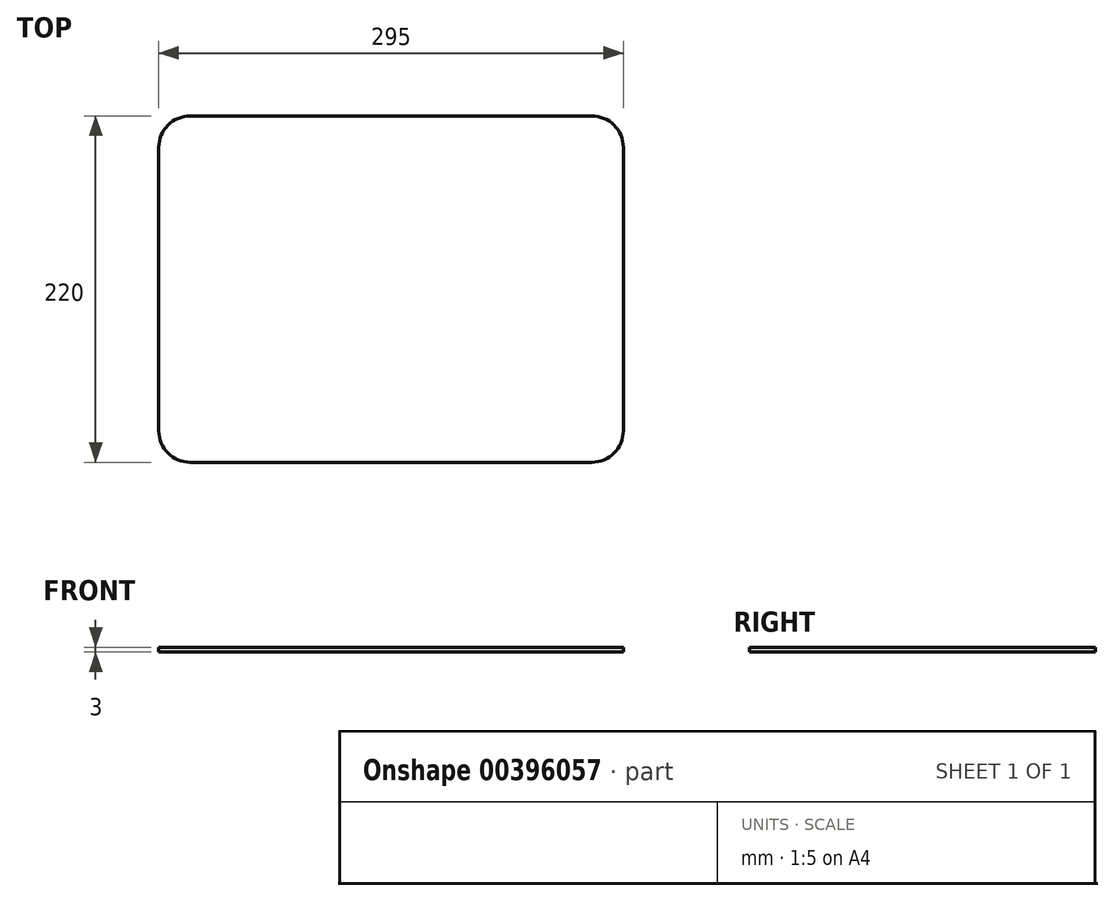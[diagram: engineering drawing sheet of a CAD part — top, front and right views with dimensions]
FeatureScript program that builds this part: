
annotation { "Feature Type Name" : "Feature", "Feature Type Description" : "" }
export const myFeature = defineFeature(function(context is Context, id is Id, definition is map)
    precondition{}
    {
        {
            var Q0;
            Q0=qCreatedBy(makeId("Top.planeOp"),FACE);
            var sketch = newSketch(context, id + "F0", { "sketchPlane" : qUnion([Q0])});
            skLineSegment(sketch, "E0.bottom", {"start": v(-127.5, 110) * mm, "end": v(127.5, 110) * mm});
            skLineSegment(sketch, "E0.top", {"start": v(-127.5, -110) * mm, "end": v(127.5, -110) * mm});
            skLineSegment(sketch, "E0.left", {"start": v(-147.5, 90) * mm, "end": v(-147.5, -90) * mm});
            skLineSegment(sketch, "E0.right", {"start": v(147.5, 90) * mm, "end": v(147.5, -90) * mm});
            skPoint(sketch, "E0.middle", {"position": v(0, 0) * mm});
            skPoint(sketch, "E1.visualSharp", {"position": v(-147.5, 110) * mm});
            skArc(sketch, "E1.filletArc", {"start": v(-127.5, 110) * mm, "mid": v(-141.64, 104.14) * mm, "end": v(-147.5, 90) * mm});
            skPoint(sketch, "E2.visualSharp", {"position": v(-147.5, -110) * mm});
            skArc(sketch, "E2.filletArc", {"start": v(-147.5, -90) * mm, "mid": v(-141.64, -104.14) * mm, "end": v(-127.5, -110) * mm});
            skPoint(sketch, "E3.visualSharp", {"position": v(147.5, -110) * mm});
            skArc(sketch, "E3.filletArc", {"start": v(127.5, -110) * mm, "mid": v(141.64, -104.14) * mm, "end": v(147.5, -90) * mm});
            skPoint(sketch, "E4.visualSharp", {"position": v(147.5, 110) * mm});
            skArc(sketch, "E4.filletArc", {"start": v(147.5, 90) * mm, "mid": v(141.64, 104.14) * mm, "end": v(127.5, 110) * mm});
            skSolve(sketch);
        }
        {
            var Q0;
            Q0=qSketchRegion(id+"F0",true);
            extrude(context, id + "F1", {"entities" : qUnion([Q0]), "depth" : 3 * mm});
        }
    });
